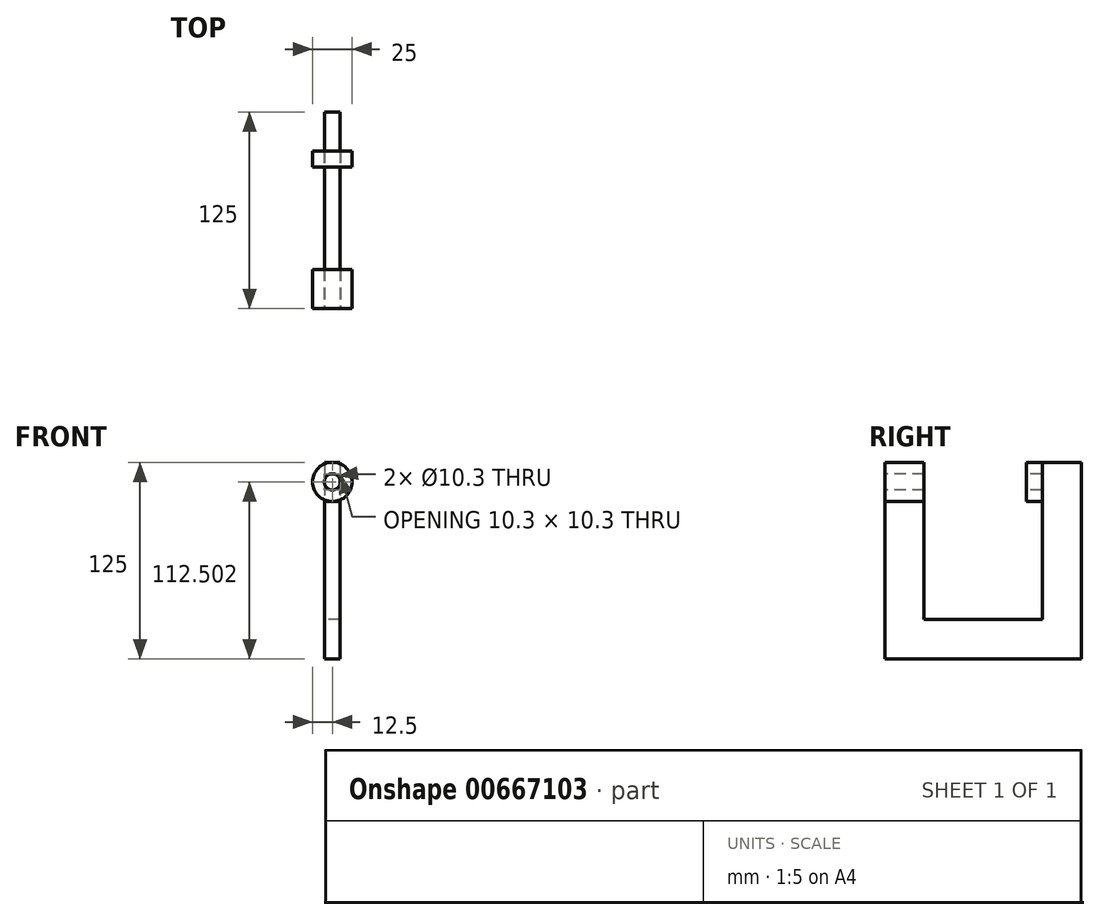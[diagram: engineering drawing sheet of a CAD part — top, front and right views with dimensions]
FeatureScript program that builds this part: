
annotation { "Feature Type Name" : "Feature", "Feature Type Description" : "" }
export const myFeature = defineFeature(function(context is Context, id is Id, definition is map)
    precondition{}
    {
        {
            var Q0;
            Q0=qCreatedBy(makeId("Right.planeOp"),FACE);
            var sketch = newSketch(context, id + "F0", { "sketchPlane" : qUnion([Q0])});
            skLineSegment(sketch, "E0", {"start": v(-109.86, 70.87) * mm, "end": v(-109.86, -29.13) * mm});
            skLineSegment(sketch, "E1", {"start": v(15.14, 95.87) * mm, "end": v(15.14, -29.13) * mm});
            skLineSegment(sketch, "E2", {"start": v(15.14, 95.87) * mm, "end": v(-9.86, 95.87) * mm});
            skLineSegment(sketch, "E3", {"start": v(-9.86, 95.87) * mm, "end": v(-9.86, -4.13) * mm});
            skLineSegment(sketch, "E4", {"start": v(-9.86, -4.13) * mm, "end": v(-84.86, -4.13) * mm});
            skLineSegment(sketch, "E5", {"start": v(-84.86, -4.13) * mm, "end": v(-84.86, 70.87) * mm});
            skLineSegment(sketch, "E6", {"start": v(-84.86, 70.87) * mm, "end": v(-109.86, 70.87) * mm});
            skLineSegment(sketch, "E7", {"start": v(-109.86, -29.13) * mm, "end": v(15.14, -29.13) * mm});
            skSolve(sketch);
        }
        {
            var Q0;
            Q0=qSketchRegion(id+"F0",true);
            extrude(context, id + "F1", {"entities" : qUnion([Q0]), "endBound" : BoundingType.SYMMETRIC, "depth" : 10 * mm, "offsetDistance" : 25 * mm});
        }
        {
            var Q0;
            Q0=makeQuery(id+"F1.opExtrude","SWEPT_FACE",FACE,{"disambiguationData":[OSD([sQuery(id+"F0.wireOp",EDGE,"E3")])]});
            var sketch = newSketch(context, id + "F2", { "sketchPlane" : qUnion([Q0])});
            skCircle(sketch, "E8", {"center": v(0, 83.37) * mm, "radius": 12.5 * mm});
            skSolve(sketch);
        }
        {
            var Q0;
            Q0=qSketchRegion(id+"F2",true);
            extrude(context, id + "F3", {"entities" : qUnion([Q0]), "depth" : 100 * mm, "offsetDistance" : 25 * mm});
        }
        {
            var Q0;
            Q0=qCreatedBy(makeId("Right.planeOp"),FACE);
            var sketch = newSketch(context, id + "F4", { "sketchPlane" : qUnion([Q0])});
            skLineSegment(sketch, "E9.bottom", {"start": v(-84.86, 0.87) * mm, "end": v(-19.86, 0.87) * mm});
            skLineSegment(sketch, "E9.top", {"start": v(-84.86, 100.87) * mm, "end": v(-19.86, 100.87) * mm});
            skLineSegment(sketch, "E9.left", {"start": v(-84.86, 0.87) * mm, "end": v(-84.86, 100.87) * mm});
            skLineSegment(sketch, "E9.right", {"start": v(-19.86, 0.87) * mm, "end": v(-19.86, 100.87) * mm});
            skSolve(sketch);
        }
        {
            var Q0;
            Q0=qSketchRegion(id+"F4",true);
            extrude(context, id + "F5", {"entities" : qUnion([Q0]), "operationType" : NewBodyOperationType.REMOVE, "endBound" : BoundingType.SYMMETRIC, "oppositeDirection" : true, "depth" : 25 * mm, "offsetDistance" : 25 * mm});
        }
        {
            var Q0;
            Q0=makeQuery(id+"F3.opExtrude","CAP_FACE",FACE,{"disambiguationData":[OSD([sQuery(id+"F2.wireOp",EDGE,"E8")])],"isStart":false});
            var sketch = newSketch(context, id + "F6", { "sketchPlane" : qUnion([Q0])});
            skLineSegment(sketch, "E10", {"start": v(0, 83.37) * mm, "end": v(0, 95.87) * mm, "construction": true});
            skSolve(sketch);
        }
        {
            var Q0;
            Q0=sQuery(id+"F6.wireOp",VERTEX,"E10.start");
            var Q1;
            Q1=makeQuery(id+"F5.boolean.opBoolean","SPLIT",BODY,{"disambiguationData":[OD(1.0)],"derivedFrom":makeQuery(id+"F3.opExtrude","SWEPT_BODY",BODY,{"disambiguationData":[OSD([sQuery(id+"F2.wireOp",EDGE,"E8")])]})});
            hole(context, id + "F7", {"style" : HoleStyle.SIMPLE, "endStyle" : HoleEndStyle.THROUGH, "standardTappedOrClearance" : lookupTablePath({ "standard" : "ISO", "engagement" : "75%", "pitch" : "1.75 mm", "size" : "M12", "type" : "Tapped" }), "standardBlindInLast" : lookupTablePath({ "standard" : "ISO", "engagement" : "75%", "pitch" : "1.75 mm", "size" : "M12", "type" : "Tapped" }), "holeDiameter" : 10.3 * mm, "majorDiameter" : 12 * mm, "showTappedDepth" : true, "isTappedThrough" : true, "tappedDepth" : 12 * mm, "tapClearance" : 3, "locations" : qUnion([Q0]), "scope" : qUnion([Q1])});
        }
    });
